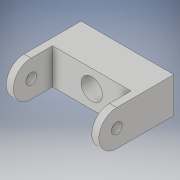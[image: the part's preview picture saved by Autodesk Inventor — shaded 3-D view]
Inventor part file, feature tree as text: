
AUTODESK INVENTOR PART (.ipt)
format: ipt  version: 2019 (Build 230136000, 136)  size: 135,168 bytes
history: native  units: mm
features: extrude x4, sketch x4, other x1
ambient origin geometry x8: Origin, YZ Plane, XZ Plane, XY Plane, X Axis, Y Axis, Z Axis, Center Point
bodies: Body1 (feature_tree)
feature tree (9):
  other  "Sólido1"
  extrude  "Extrusión1"  Depth=50.0mm
  extrude  "Extrusión2"  Depth=50.0mm
  extrude  "Extrusión3"  Depth=15.0mm
  extrude  "Extrusión4"  Depth=10.0mm TaperAngle=0.0deg
  sketch  "Boceto1"  dims[d0=130.0mm d1=50.0mm]
  sketch  "Boceto2"  dims[d2=50.0mm d3=0.0mm d4=30.0mm]
  sketch  "Boceto3"  dims[d5=30.0mm d6=15.0mm]
  sketch  "Boceto4"  dims[d7=10.0mm d8=0.0mm d9=10.0mm d10=0.0mm d11=30.0mm d12=10.0mm d13=0.0mm]
